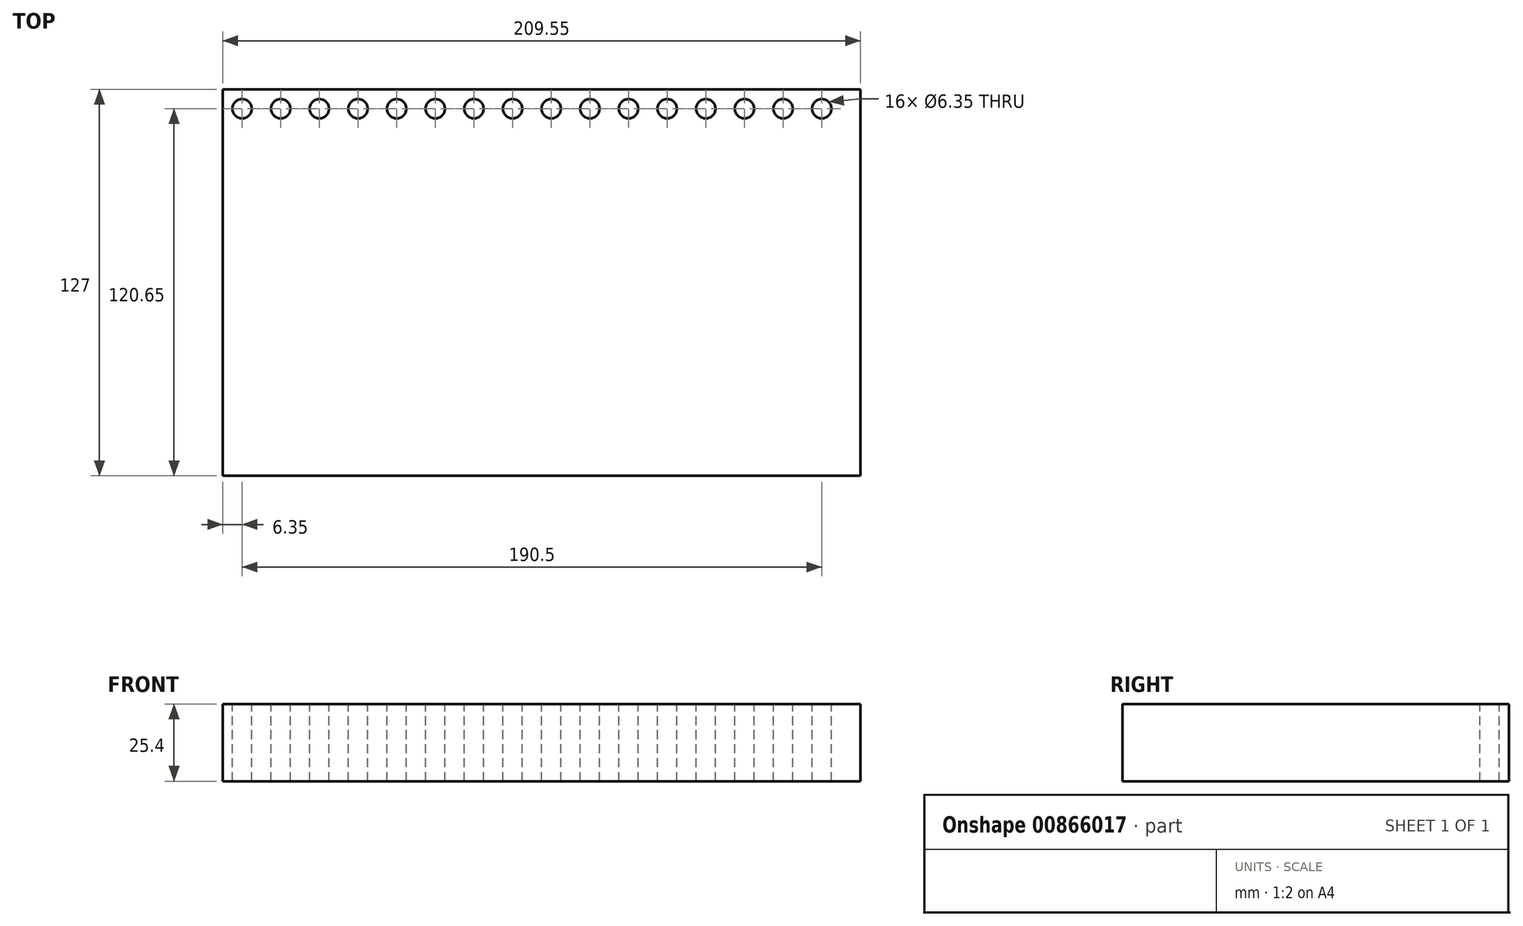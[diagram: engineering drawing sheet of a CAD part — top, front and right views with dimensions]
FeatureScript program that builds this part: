
annotation { "Feature Type Name" : "Feature", "Feature Type Description" : "" }
export const myFeature = defineFeature(function(context is Context, id is Id, definition is map)
    precondition{}
    {
        {
            var Q0;
            Q0=qCreatedBy(makeId("Front.planeOp"),FACE);
            var sketch = newSketch(context, id + "F0", { "sketchPlane" : qUnion([Q0])});
            skLineSegment(sketch, "E0.bottom", {"start": v(0, 0) * mm, "end": v(209.55, 0) * mm});
            skLineSegment(sketch, "E0.top", {"start": v(0, 25.4) * mm, "end": v(209.55, 25.4) * mm});
            skLineSegment(sketch, "E0.left", {"start": v(0, 0) * mm, "end": v(0, 25.4) * mm});
            skLineSegment(sketch, "E0.right", {"start": v(209.55, 0) * mm, "end": v(209.55, 25.4) * mm});
            skSolve(sketch);
        }
        {
            var Q0;
            Q0 = qSketchRegion(id + "F0", true);
            extrude(context, id + "F1", {"entities" : qUnion([Q0]), "depth" : 127 * mm, "offsetDistance" : 25.4 * mm});
        }
        {
            var Q0;
            Q0=makeQuery(id+"F1.opExtrude","SWEPT_FACE",FACE,{"disambiguationData":[OSD([sQuery(id+"F0.wireOp",EDGE,"E0.top")])]});
            var sketch = newSketch(context, id + "F2", { "sketchPlane" : qUnion([Q0])});
            skCircle(sketch, "E1", {"center": v(6.35, -6.35) * mm, "radius": 3.18 * mm});
            skCircle(sketch, "E2.1.0.0", {"center": v(19.05, -6.35) * mm, "radius": 3.18 * mm});
            skCircle(sketch, "E2.2.0.0", {"center": v(31.75, -6.35) * mm, "radius": 3.18 * mm});
            skCircle(sketch, "E2.3.0.0", {"center": v(44.45, -6.35) * mm, "radius": 3.18 * mm});
            skCircle(sketch, "E2.4.0.0", {"center": v(57.15, -6.35) * mm, "radius": 3.18 * mm});
            skCircle(sketch, "E2.5.0.0", {"center": v(69.85, -6.35) * mm, "radius": 3.18 * mm});
            skCircle(sketch, "E2.6.0.0", {"center": v(82.55, -6.35) * mm, "radius": 3.18 * mm});
            skCircle(sketch, "E2.7.0.0", {"center": v(95.25, -6.35) * mm, "radius": 3.18 * mm});
            skCircle(sketch, "E2.8.0.0", {"center": v(107.95, -6.35) * mm, "radius": 3.18 * mm});
            skCircle(sketch, "E2.9.0.0", {"center": v(120.65, -6.35) * mm, "radius": 3.18 * mm});
            skCircle(sketch, "E2.10.0.0", {"center": v(133.35, -6.35) * mm, "radius": 3.18 * mm});
            skCircle(sketch, "E2.11.0.0", {"center": v(146.05, -6.35) * mm, "radius": 3.18 * mm});
            skCircle(sketch, "E2.12.0.0", {"center": v(158.75, -6.35) * mm, "radius": 3.18 * mm});
            skCircle(sketch, "E2.13.0.0", {"center": v(171.45, -6.35) * mm, "radius": 3.18 * mm});
            skCircle(sketch, "E2.14.0.0", {"center": v(184.15, -6.35) * mm, "radius": 3.18 * mm});
            skCircle(sketch, "E2.15.0.0", {"center": v(196.85, -6.35) * mm, "radius": 3.18 * mm});
            skLineSegment(sketch, "E2.direction1", {"start": v(6.35, -6.35) * mm, "end": v(19.05, -6.35) * mm, "construction": true});
            skSolve(sketch);
        }
        {
            var Q0;
            Q0=sQuery(id+"F2.wireOp",VERTEX,"E1.center");
            var Q1;
            Q1=sQuery(id+"F2.wireOp",VERTEX,"E2.direction1.end");
            var Q2;
            Q2=sQuery(id+"F2.wireOp",VERTEX,"E2.2.0.0.center");
            var Q3;
            Q3=sQuery(id+"F2.wireOp",VERTEX,"E2.3.0.0.center");
            var Q4;
            Q4=sQuery(id+"F2.wireOp",VERTEX,"E2.4.0.0.center");
            var Q5;
            Q5=sQuery(id+"F2.wireOp",VERTEX,"E2.5.0.0.center");
            var Q6;
            Q6=sQuery(id+"F2.wireOp",VERTEX,"E2.6.0.0.center");
            var Q7;
            Q7=sQuery(id+"F2.wireOp",VERTEX,"E2.7.0.0.center");
            var Q8;
            Q8=sQuery(id+"F2.wireOp",VERTEX,"E2.8.0.0.center");
            var Q9;
            Q9=sQuery(id+"F2.wireOp",VERTEX,"E2.9.0.0.center");
            var Q10;
            Q10=sQuery(id+"F2.wireOp",VERTEX,"E2.10.0.0.center");
            var Q11;
            Q11=sQuery(id+"F2.wireOp",VERTEX,"E2.11.0.0.center");
            var Q12;
            Q12=sQuery(id+"F2.wireOp",VERTEX,"E2.12.0.0.center");
            var Q13;
            Q13=sQuery(id+"F2.wireOp",VERTEX,"E2.13.0.0.center");
            var Q14;
            Q14=sQuery(id+"F2.wireOp",VERTEX,"E2.14.0.0.center");
            var Q15;
            Q15=sQuery(id+"F2.wireOp",VERTEX,"E2.15.0.0.center");
            var Q16;
            Q16=makeQuery(id+"F1.opExtrude","SWEPT_BODY",BODY,{"disambiguationData":[OSD([sQuery(id+"F0.wireOp",EDGE,"E0.bottom"),sQuery(id+"F0.wireOp",EDGE,"E0.top"),sQuery(id+"F0.wireOp",EDGE,"E0.left"),sQuery(id+"F0.wireOp",EDGE,"E0.right")])]});
            hole(context, id + "F3", {"style" : HoleStyle.SIMPLE, "endStyle" : HoleEndStyle.THROUGH, "holeDiameter" : 6.35 * mm, "majorDiameter" : 6.35 * mm, "isTappedThrough" : true, "tappedDepth" : 12.7 * mm, "tapClearance" : 3, "locations" : qUnion([Q0, Q1, Q2, Q3, Q4, Q5, Q6, Q7, Q8, Q9, Q10, Q11, Q12, Q13, Q14, Q15]), "scope" : qUnion([Q16])});
        }
    });
